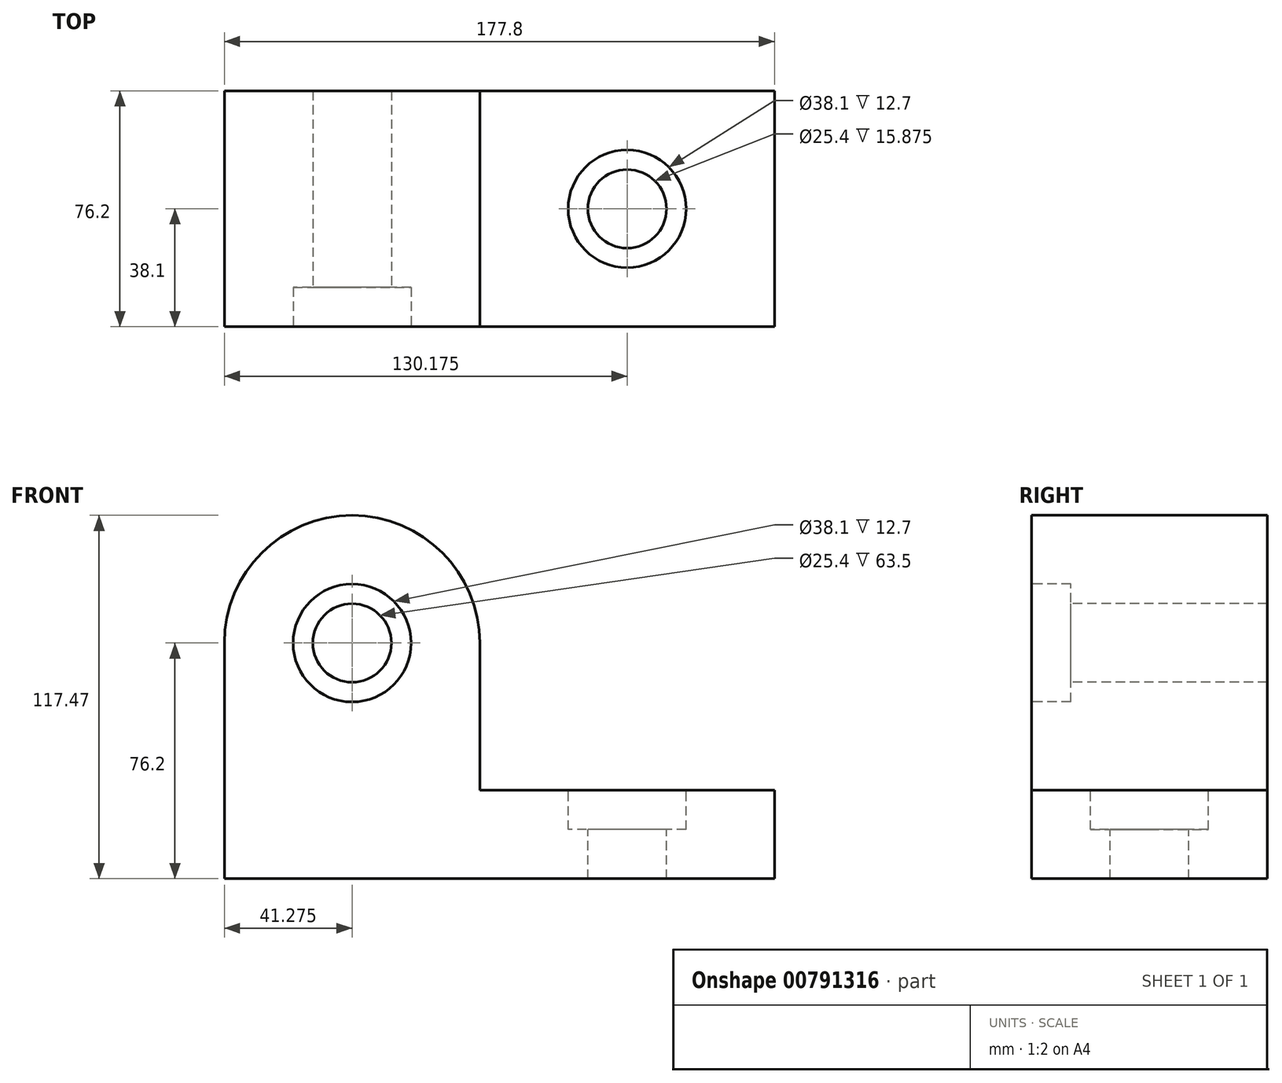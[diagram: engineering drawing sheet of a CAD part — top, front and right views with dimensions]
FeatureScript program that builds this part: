
annotation { "Feature Type Name" : "Feature", "Feature Type Description" : "" }
export const myFeature = defineFeature(function(context is Context, id is Id, definition is map)
    precondition{}
    {
        {
            var Q0;
            Q0=qCreatedBy(makeId("Front.planeOp"),FACE);
            var sketch = newSketch(context, id + "F0", { "sketchPlane" : qUnion([Q0])});
            skLineSegment(sketch, "E0", {"start": v(0, 0) * mm, "end": v(177.8, 0) * mm});
            skLineSegment(sketch, "E1", {"start": v(177.8, 0) * mm, "end": v(177.8, 28.58) * mm});
            skLineSegment(sketch, "E2", {"start": v(177.8, 28.58) * mm, "end": v(82.55, 28.58) * mm});
            skLineSegment(sketch, "E3", {"start": v(82.55, 28.58) * mm, "end": v(82.55, 155.57) * mm});
            skLineSegment(sketch, "E4", {"start": v(82.55, 155.57) * mm, "end": v(0, 155.57) * mm});
            skLineSegment(sketch, "E5", {"start": v(0, 155.57) * mm, "end": v(0, 0) * mm});
            skSolve(sketch);
        }
        {
            var Q0;
            Q0=makeQuery(id+"F0.imprint","IMPRINT",FACE,{"disambiguationData":[TD([[makeQuery(id+"F0.imprint","IMPRINT",EDGE,{"derivedFrom":sQuery(id+"F0.wireOp",EDGE,"E0")}),1.0]])]});
            extrude(context, id + "F1", {"entities" : qUnion([Q0]), "depth" : 76.2 * mm, "offsetDistance" : 25.4 * mm});
        }
        {
            var Q0;
            Q0=makeQuery(id+"F1.opExtrude","CAP_FACE",FACE,{"disambiguationData":[OSD([sQuery(id+"F0.wireOp",EDGE,"E0"),sQuery(id+"F0.wireOp",EDGE,"E1"),sQuery(id+"F0.wireOp",EDGE,"E2"),sQuery(id+"F0.wireOp",EDGE,"E3"),sQuery(id+"F0.wireOp",EDGE,"E4"),sQuery(id+"F0.wireOp",EDGE,"E5")])],"isStart":false});
            var sketch = newSketch(context, id + "F2", { "sketchPlane" : qUnion([Q0])});
            skLineSegment(sketch, "E6", {"start": v(0, 0) * mm, "end": v(0, 76.2) * mm, "construction": true});
            skLineSegment(sketch, "E7", {"start": v(0, 76.2) * mm, "end": v(82.55, 76.2) * mm, "construction": true});
            skArc(sketch, "E8", {"start": v(82.55, 76.2) * mm, "mid": v(41.28, 117.48) * mm, "end": v(0, 76.2) * mm});
            skSolve(sketch);
        }
        {
            var Q0;
            {var subQ0=sQuery(id+"F2.wireOp",EDGE,"E8");Q0=makeQuery(id+"F2.imprint","IMPRINT",FACE,{"disambiguationData":[TD([[makeQuery(id+"F2.imprint","IMPRINT",EDGE,{"derivedFrom":subQ0}),-1.0]])]});}
            extrude(context, id + "F3", {"entities" : qUnion([Q0]), "operationType" : NewBodyOperationType.REMOVE, "endBound" : BoundingType.UP_TO_NEXT, "oppositeDirection" : true, "depth" : 25.4 * mm, "offsetDistance" : 25.4 * mm});
        }
        {
            var Q0;
            Q0=makeQuery(id+"F1.opExtrude","CAP_FACE",FACE,{"disambiguationData":[OSD([sQuery(id+"F0.wireOp",EDGE,"E0"),sQuery(id+"F0.wireOp",EDGE,"E1"),sQuery(id+"F0.wireOp",EDGE,"E2"),sQuery(id+"F0.wireOp",EDGE,"E3"),sQuery(id+"F0.wireOp",EDGE,"E4"),sQuery(id+"F0.wireOp",EDGE,"E5")])],"isStart":false});
            var sketch = newSketch(context, id + "F4", { "sketchPlane" : qUnion([Q0])});
            skLineSegment(sketch, "E9", {"start": v(0, 0) * mm, "end": v(0, 76.2) * mm, "construction": true});
            skLineSegment(sketch, "E10", {"start": v(0, 76.2) * mm, "end": v(82.55, 76.2) * mm, "construction": true});
            skCircle(sketch, "E11", {"center": v(41.28, 76.2) * mm, "radius": 19.05 * mm});
            skSolve(sketch);
        }
        {
            var Q0;
            Q0=makeQuery(id+"F4.imprint","IMPRINT",FACE,{"disambiguationData":[TD([[makeQuery(id+"F4.imprint","IMPRINT",EDGE,{"derivedFrom":sQuery(id+"F4.wireOp",EDGE,"E11")}),1.0]])]});
            extrude(context, id + "F5", {"entities" : qUnion([Q0]), "operationType" : NewBodyOperationType.REMOVE, "oppositeDirection" : true, "depth" : 12.7 * mm, "offsetDistance" : 25.4 * mm});
        }
        {
            var Q0;
            Q0=makeQuery(id+"F5.boolean.opBoolean","COPY",FACE,{"derivedFrom":makeQuery(id+"F5.opExtrude","CAP_FACE",FACE,{"disambiguationData":[OSD([sQuery(id+"F4.wireOp",EDGE,"E11")])],"isStart":false})});
            var sketch = newSketch(context, id + "F6", { "sketchPlane" : qUnion([Q0])});
            skCircle(sketch, "E12", {"center": v(41.28, 76.2) * mm, "radius": 12.7 * mm});
            skSolve(sketch);
        }
        {
            var Q0;
            Q0=makeQuery(id+"F6.imprint","IMPRINT",FACE,{"disambiguationData":[TD([[makeQuery(id+"F6.imprint","IMPRINT",EDGE,{"derivedFrom":sQuery(id+"F6.wireOp",EDGE,"E12")}),1.0]])]});
            extrude(context, id + "F7", {"entities" : qUnion([Q0]), "operationType" : NewBodyOperationType.REMOVE, "endBound" : BoundingType.UP_TO_NEXT, "oppositeDirection" : true, "depth" : 25.4 * mm, "offsetDistance" : 25.4 * mm});
        }
        {
            var Q0;
            Q0=makeQuery(id+"F1.opExtrude","SWEPT_FACE",FACE,{"disambiguationData":[OSD([sQuery(id+"F0.wireOp",EDGE,"E2")])]});
            var sketch = newSketch(context, id + "F8", { "sketchPlane" : qUnion([Q0])});
            skLineSegment(sketch, "E13", {"start": v(177.8, 0) * mm, "end": v(130.18, 0) * mm, "construction": true});
            skLineSegment(sketch, "E14", {"start": v(130.18, 0) * mm, "end": v(130.18, -76.2) * mm, "construction": true});
            skCircle(sketch, "E15", {"center": v(130.18, -38.1) * mm, "radius": 19.05 * mm});
            skSolve(sketch);
        }
        {
            var Q0;
            Q0=makeQuery(id+"F8.imprint","IMPRINT",FACE,{"disambiguationData":[TD([[makeQuery(id+"F8.imprint","IMPRINT",EDGE,{"derivedFrom":sQuery(id+"F8.wireOp",EDGE,"E15")}),1.0]])]});
            extrude(context, id + "F9", {"entities" : qUnion([Q0]), "operationType" : NewBodyOperationType.REMOVE, "oppositeDirection" : true, "depth" : 12.7 * mm, "offsetDistance" : 25.4 * mm});
        }
        {
            var Q0;
            Q0=makeQuery(id+"F9.boolean.opBoolean","COPY",FACE,{"derivedFrom":makeQuery(id+"F9.opExtrude","CAP_FACE",FACE,{"disambiguationData":[OSD([sQuery(id+"F8.wireOp",EDGE,"E15")])],"isStart":false})});
            var sketch = newSketch(context, id + "F10", { "sketchPlane" : qUnion([Q0])});
            skCircle(sketch, "E16", {"center": v(130.18, -38.1) * mm, "radius": 12.7 * mm});
            skSolve(sketch);
        }
        {
            var Q0;
            Q0=makeQuery(id+"F10.imprint","IMPRINT",FACE,{"disambiguationData":[TD([[makeQuery(id+"F10.imprint","IMPRINT",EDGE,{"derivedFrom":sQuery(id+"F10.wireOp",EDGE,"E16")}),1.0]])]});
            extrude(context, id + "F11", {"entities" : qUnion([Q0]), "operationType" : NewBodyOperationType.REMOVE, "endBound" : BoundingType.UP_TO_NEXT, "oppositeDirection" : true, "depth" : 25.4 * mm, "offsetDistance" : 25.4 * mm});
        }
    });
